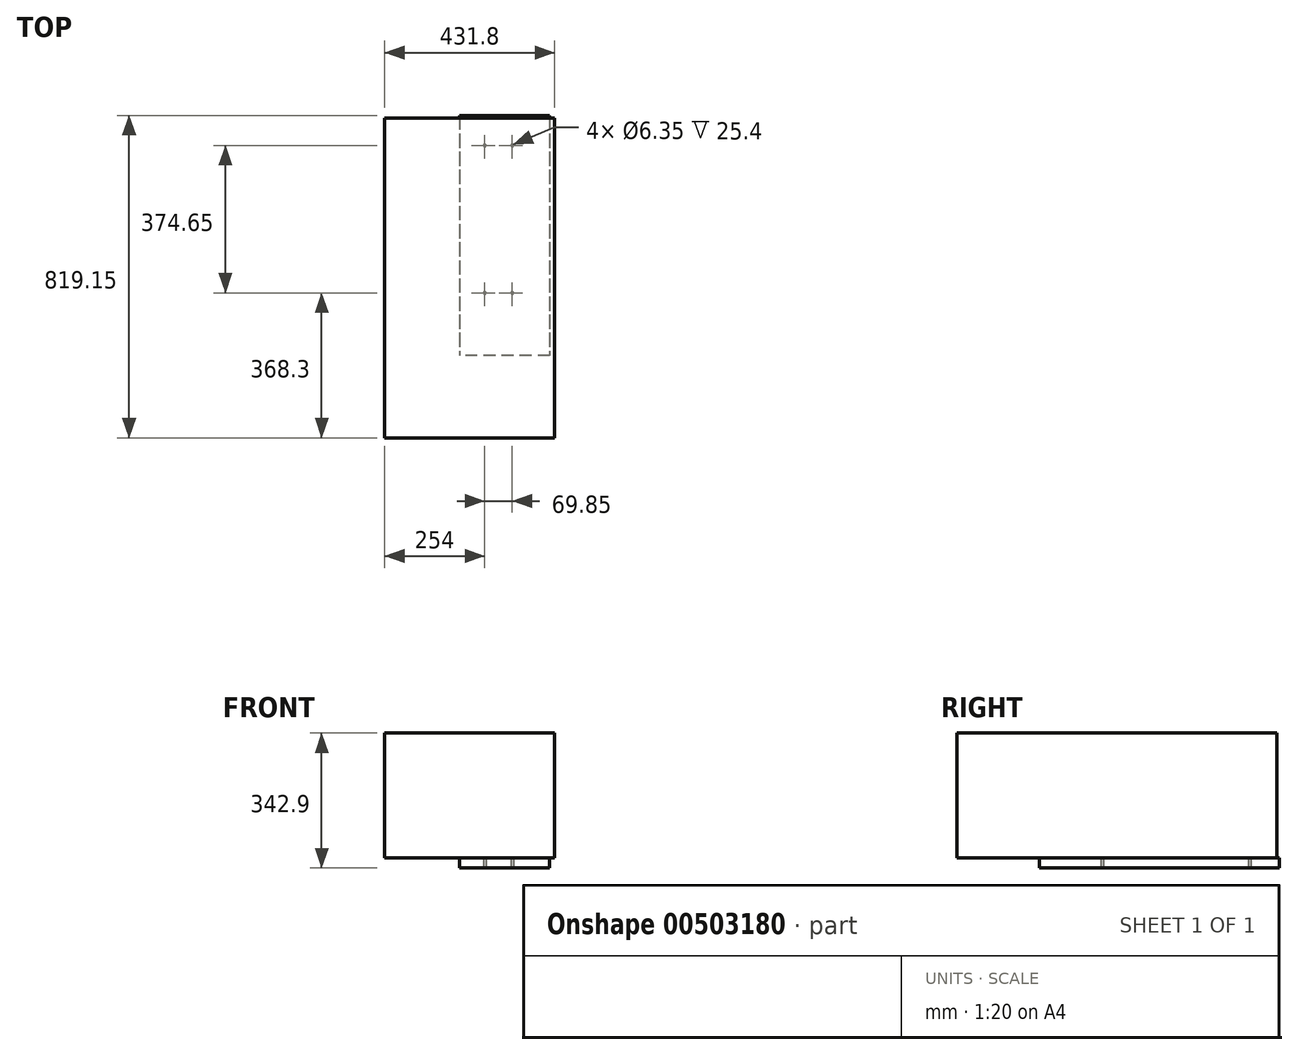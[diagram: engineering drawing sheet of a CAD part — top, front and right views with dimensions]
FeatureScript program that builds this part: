
annotation { "Feature Type Name" : "Feature", "Feature Type Description" : "" }
export const myFeature = defineFeature(function(context is Context, id is Id, definition is map)
    precondition{}
    {
        {
            var Q0;
            Q0=qCreatedBy(makeId("Top.planeOp"),FACE);
            var sketch = newSketch(context, id + "F0", { "sketchPlane" : qUnion([Q0])});
            skLineSegment(sketch, "E0.bottom", {"start": v(114.3, 304.8) * mm, "end": v(-114.3, 304.8) * mm});
            skLineSegment(sketch, "E0.top", {"start": v(114.3, -304.8) * mm, "end": v(-114.3, -304.8) * mm});
            skLineSegment(sketch, "E0.left", {"start": v(114.3, 304.8) * mm, "end": v(114.3, -304.8) * mm});
            skLineSegment(sketch, "E0.right", {"start": v(-114.3, 304.8) * mm, "end": v(-114.3, -304.8) * mm});
            skPoint(sketch, "E0.middle", {"position": v(0, 0) * mm});
            skSolve(sketch);
        }
        {
            var Q0;
            Q0 = qSketchRegion(id + "F0", true);
            extrude(context, id + "F1", {"entities" : qUnion([Q0]), "depth" : 25.4 * mm});
        }
        {
            var Q0;
            Q0=makeQuery(id+"F1.opExtrude","CAP_FACE",FACE,{"disambiguationData":[OSD([sQuery(id+"F0.wireOp",EDGE,"E0.bottom"),sQuery(id+"F0.wireOp",EDGE,"E0.top"),sQuery(id+"F0.wireOp",EDGE,"E0.left"),sQuery(id+"F0.wireOp",EDGE,"E0.right")])],"isStart":false});
            var sketch = newSketch(context, id + "F2", { "sketchPlane" : qUnion([Q0])});
            skLineSegment(sketch, "E1.bottom", {"start": v(127, -514.35) * mm, "end": v(-304.8, -514.35) * mm});
            skLineSegment(sketch, "E1.top", {"start": v(127, 298.45) * mm, "end": v(-304.8, 298.45) * mm});
            skLineSegment(sketch, "E1.left", {"start": v(127, -514.35) * mm, "end": v(127, 298.45) * mm});
            skLineSegment(sketch, "E1.right", {"start": v(-304.8, -514.35) * mm, "end": v(-304.8, 298.45) * mm});
            skPoint(sketch, "E1.middle", {"position": v(0, -101.6) * mm});
            skSolve(sketch);
        }
        {
            var Q0;
            Q0 = qSketchRegion(id + "F2", true);
            extrude(context, id + "F3", {"entities" : qUnion([Q0]), "operationType" : NewBodyOperationType.ADD, "depth" : 317.5 * mm});
        }
        {
            var Q0;
            Q0=makeQuery(id+"F1.opExtrude","CAP_FACE",FACE,{"disambiguationData":[OSD([sQuery(id+"F0.wireOp",EDGE,"E0.bottom"),sQuery(id+"F0.wireOp",EDGE,"E0.top"),sQuery(id+"F0.wireOp",EDGE,"E0.left"),sQuery(id+"F0.wireOp",EDGE,"E0.right")])],"isStart":true});
            var sketch = newSketch(context, id + "F4", { "sketchPlane" : qUnion([Q0])});
            skCircle(sketch, "E2", {"center": v(-50.8, -228.6) * mm, "radius": 3.18 * mm});
            skCircle(sketch, "E3", {"center": v(19.05, -228.6) * mm, "radius": 3.18 * mm});
            skCircle(sketch, "E4", {"center": v(-50.8, 146.05) * mm, "radius": 3.18 * mm});
            skCircle(sketch, "E5", {"center": v(19.05, 146.05) * mm, "radius": 3.18 * mm});
            skSolve(sketch);
        }
        {
            var Q0;
            Q0 = qSketchRegion(id + "F4", true);
            extrude(context, id + "F5", {"entities" : qUnion([Q0]), "operationType" : NewBodyOperationType.REMOVE, "oppositeDirection" : true, "depth" : 25.4 * mm});
        }
    });
